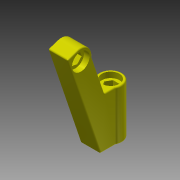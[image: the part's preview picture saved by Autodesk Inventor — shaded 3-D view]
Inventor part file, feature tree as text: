
AUTODESK INVENTOR PART (.ipt)
format: ipt  version: 2013 (Build 170138000, 138)  size: 222,208 bytes
history: native  units: mm
features: extrude x9, sketch x7, fillet x1
ambient origin geometry x8: Origin, YZ Plane, XZ Plane, XY Plane, X Axis, Y Axis, Z Axis, Center Point
bodies: Solid1 (feature_tree)
feature tree (17):
  extrude  "Extrusion1"  Depth=62.5mm
  extrude  "Extrusion2"  Depth=25.0mm TaperAngle=0.0deg
  extrude  "Extrusion3"  Depth=22.1mm
  extrude  "Extrusion4"  Depth=7.0mm TaperAngle=0.0deg
  extrude  "Extrusion5"  Depth=7.0mm TaperAngle=0.0deg
  extrude  "Extrusion7"  Depth=20.0mm
  extrude  "Extrusion8"  Depth=3.0mm
  extrude  "Extrusion9"  Depth=10.0mm TaperAngle=0.0deg
  extrude  "Extrusion10"  Depth=1.5mm
  fillet  "Fillet3"  Radius=15.1mm
  sketch  "Sketch1"  dims[d4=25.0mm d6=62.5mm]
  sketch  "Sketch2"  dims[d7=25.0mm d8=0.0mm d9=25.0mm d10=0.0mm]
  sketch  "Sketch3"  dims[d13=25.0mm d14=0.0mm d15=22.1mm]
  sketch  "Sketch4"  dims[d17=7.0mm d18=0.0mm d19=7.0mm d20=0.0mm]
  sketch  "Sketch7"  dims[d32=22.1mm d34=7.0mm d35=0.0mm]
  sketch  "Sketch8"  dims[d36=7.0mm d37=0.0mm d41=20.0mm]
  sketch  "Sketch10"  dims[d43=10.0mm d44=0.0mm d46=3.0mm d47=10.0mm d48=0.0mm d50=1.5mm d51=15.1mm d53=8.5mm d54=14.0mm d55=3.0mm d56=50.0mm d57=50.0mm d58=14.0mm]
